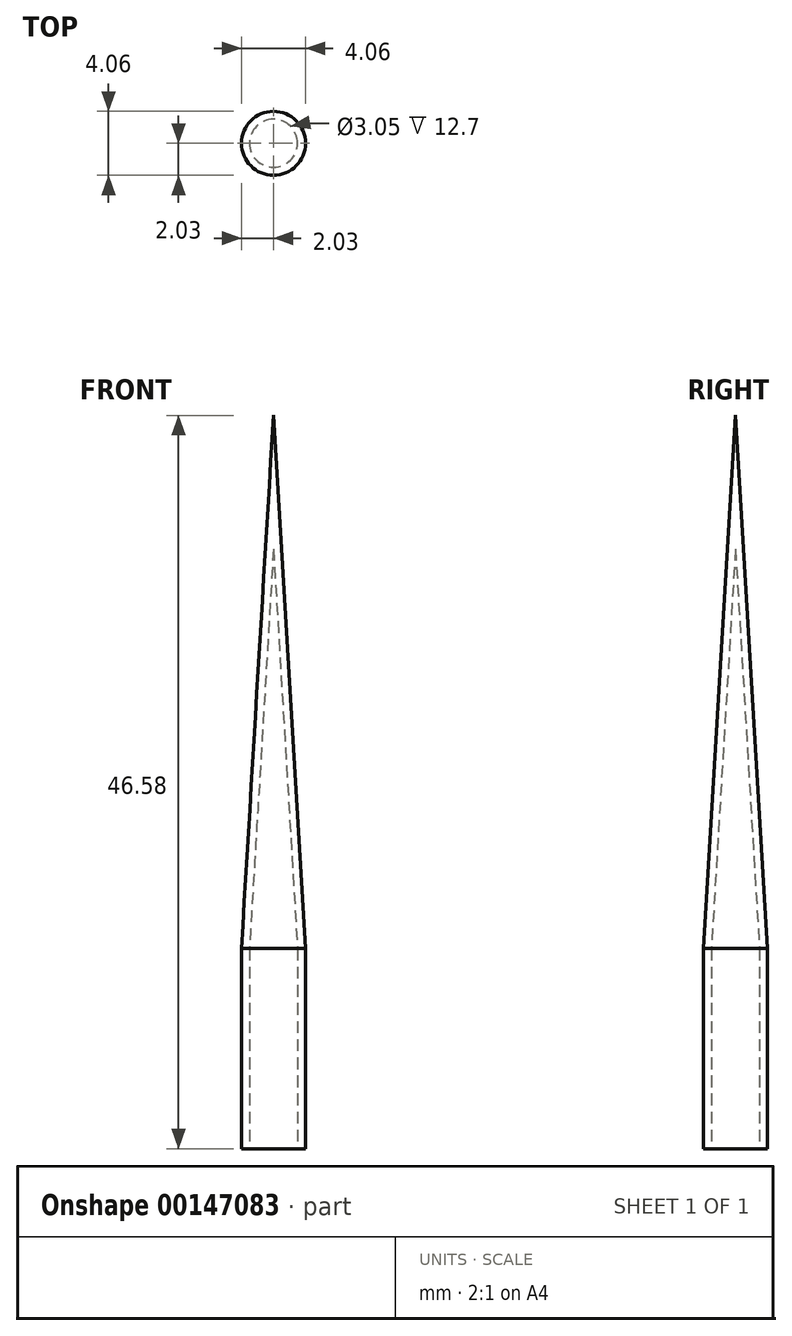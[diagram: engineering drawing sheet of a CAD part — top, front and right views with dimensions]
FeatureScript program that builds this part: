
annotation { "Feature Type Name" : "Feature", "Feature Type Description" : "" }
export const myFeature = defineFeature(function(context is Context, id is Id, definition is map)
    precondition{}
    {
        {
            var Q0;
            Q0=qCreatedBy(makeId("Front.planeOp"),FACE);
            var sketch = newSketch(context, id + "F0", { "sketchPlane" : qUnion([Q0])});
            skLineSegment(sketch, "E0", {"start": v(0, 0) * mm, "end": v(0, 63.5) * mm, "construction": true});
            skLineSegment(sketch, "E1", {"start": v(1.52, 0) * mm, "end": v(1.52, 12.7) * mm});
            skLineSegment(sketch, "E2", {"start": v(1.52, 12.7) * mm, "end": v(0, 38.1) * mm});
            skLineSegment(sketch, "E3.0", {"start": v(2.03, 12.72) * mm, "end": v(0, 46.58) * mm});
            skLineSegment(sketch, "E3.1", {"start": v(2.03, 0) * mm, "end": v(2.03, 12.72) * mm});
            skLineSegment(sketch, "E4", {"start": v(1.52, 0) * mm, "end": v(2.03, 0) * mm});
            skLineSegment(sketch, "E5", {"start": v(0, 46.58) * mm, "end": v(0, 38.1) * mm});
            skSolve(sketch);
        }
        {
            var Q0;
            Q0=makeQuery(id+"F0.imprint","IMPRINT",FACE,{"disambiguationData":[TD([[makeQuery(id+"F0.imprint","IMPRINT",EDGE,{"derivedFrom":sQuery(id+"F0.wireOp",EDGE,"E1")}),-1.0]])]});
            var Q1;
            Q1=sQuery(id+"F0.wireOp",EDGE,"E0");
            revolve(context, id + "F1", {"entities" : qUnion([Q0]), "axis" : qUnion([Q1]), "revolveType" : RevolveType.FULL});
        }
    });
